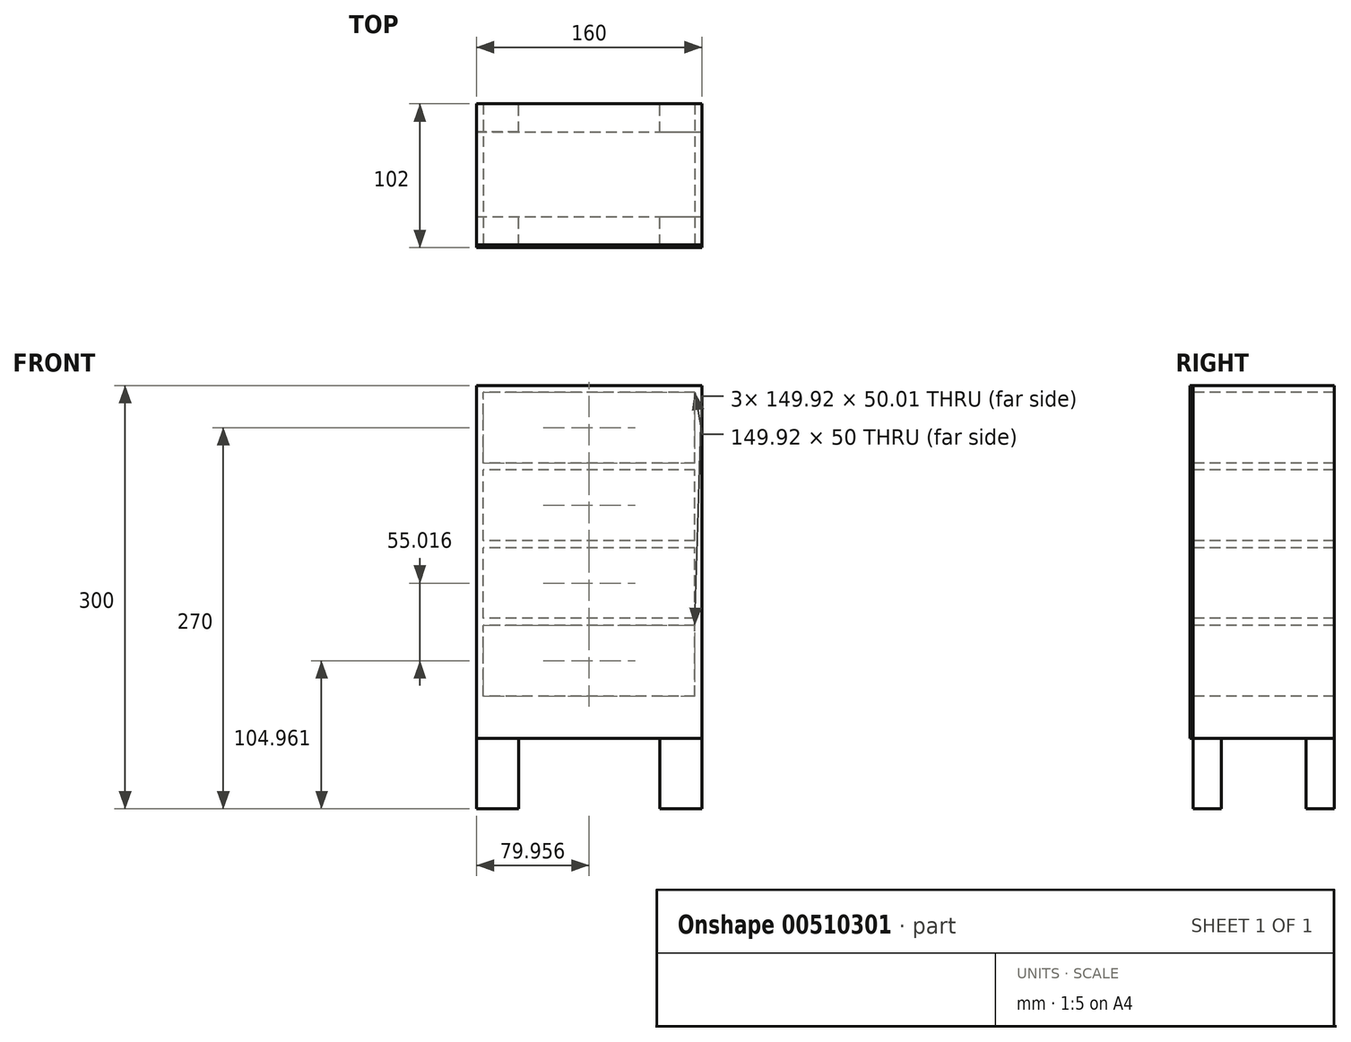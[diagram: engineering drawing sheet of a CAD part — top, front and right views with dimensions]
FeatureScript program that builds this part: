
annotation { "Feature Type Name" : "Feature", "Feature Type Description" : "" }
export const myFeature = defineFeature(function(context is Context, id is Id, definition is map)
    precondition{}
    {
        {
            var Q0;
            Q0=qCreatedBy(makeId("Front.planeOp"),FACE);
            var sketch = newSketch(context, id + "F0", { "sketchPlane" : qUnion([Q0])});
            skLineSegment(sketch, "E0.bottom", {"start": v(-78.04, -26.24) * mm, "end": v(-48.04, -26.24) * mm});
            skLineSegment(sketch, "E0.top", {"start": v(-78.04, -76.24) * mm, "end": v(-48.04, -76.24) * mm});
            skLineSegment(sketch, "E0.left", {"start": v(-78.04, -26.24) * mm, "end": v(-78.04, -76.24) * mm});
            skLineSegment(sketch, "E0.right", {"start": v(-48.04, -26.24) * mm, "end": v(-48.04, -76.24) * mm});
            skLineSegment(sketch, "E1.bottom", {"start": v(51.96, -26.2) * mm, "end": v(81.96, -26.2) * mm});
            skLineSegment(sketch, "E1.top", {"start": v(51.96, -76.21) * mm, "end": v(81.96, -76.21) * mm});
            skLineSegment(sketch, "E1.left", {"start": v(81.96, -26.2) * mm, "end": v(81.96, -76.21) * mm});
            skLineSegment(sketch, "E1.right", {"start": v(51.96, -26.2) * mm, "end": v(51.96, -76.21) * mm});
            skSolve(sketch);
        }
        {
            var Q0;
            Q0 = qSketchRegion(id + "F0", true);
            extrude(context, id + "F1", {"entities" : qUnion([Q0]), "endBound" : BoundingType.SYMMETRIC, "depth" : 100 * mm});
        }
        {
            var Q0;
            Q0=makeQuery(id+"F1.opExtrude","SWEPT_FACE",FACE,{"disambiguationData":[OSD([sQuery(id+"F0.wireOp",EDGE,"E0.bottom")])]});
            var sketch = newSketch(context, id + "F2", { "sketchPlane" : qUnion([Q0])});
            skLineSegment(sketch, "E2.bottom", {"start": v(-78.04, 50) * mm, "end": v(81.88, 50) * mm});
            skLineSegment(sketch, "E2.top", {"start": v(-78.04, -50) * mm, "end": v(81.88, -50) * mm});
            skLineSegment(sketch, "E2.left", {"start": v(-78.04, 50) * mm, "end": v(-78.04, -50) * mm});
            skLineSegment(sketch, "E2.right", {"start": v(81.88, 50) * mm, "end": v(81.88, -50) * mm});
            skSolve(sketch);
        }
        {
            var Q0;
            Q0 = qSketchRegion(id + "F2", true);
            extrude(context, id + "F3", {"entities" : qUnion([Q0]), "depth" : 250 * mm});
        }
        {
            var Q0;
            Q0=makeQuery(id+"F3.opExtrude","SWEPT_FACE",FACE,{"disambiguationData":[OSD([sQuery(id+"F2.wireOp",EDGE,"E2.top")])]});
            var sketch = newSketch(context, id + "F4", { "sketchPlane" : qUnion([Q0])});
            skLineSegment(sketch, "E3.bottom", {"start": v(-73.04, 218.76) * mm, "end": v(76.87, 218.76) * mm});
            skLineSegment(sketch, "E3.top", {"start": v(-73.04, 168.76) * mm, "end": v(76.87, 168.76) * mm});
            skLineSegment(sketch, "E3.left", {"start": v(-73.04, 218.76) * mm, "end": v(-73.04, 168.76) * mm});
            skLineSegment(sketch, "E3.right", {"start": v(76.87, 218.76) * mm, "end": v(76.87, 168.76) * mm});
            skSolve(sketch);
        }
        {
            var Q0;
            Q0=makeQuery(id+"F4.imprint","IMPRINT",FACE,{"disambiguationData":[TD([[makeQuery(id+"F4.imprint","IMPRINT",EDGE,{"derivedFrom":sQuery(id+"F4.wireOp",EDGE,"E3.bottom")}),-1.0]])]});
            extrude(context, id + "F5", {"entities" : qUnion([Q0]), "operationType" : NewBodyOperationType.REMOVE, "endBound" : BoundingType.THROUGH_ALL, "oppositeDirection" : true, "depth" : 152.4 * mm});
        }
        {
            var Q0;
            Q0=makeQuery(id+"F3.opExtrude","SWEPT_FACE",FACE,{"disambiguationData":[OSD([sQuery(id+"F2.wireOp",EDGE,"E2.top")])]});
            var sketch = newSketch(context, id + "F6", { "sketchPlane" : qUnion([Q0])});
            skLineSegment(sketch, "E4.bottom", {"start": v(-73.04, 163.76) * mm, "end": v(76.87, 163.76) * mm});
            skLineSegment(sketch, "E4.top", {"start": v(-73.04, 113.75) * mm, "end": v(76.87, 113.75) * mm});
            skLineSegment(sketch, "E4.left", {"start": v(-73.04, 163.76) * mm, "end": v(-73.04, 113.75) * mm});
            skLineSegment(sketch, "E4.right", {"start": v(76.87, 163.76) * mm, "end": v(76.87, 113.75) * mm});
            skSolve(sketch);
        }
        {
            var Q0;
            Q0=makeQuery(id+"F6.imprint","IMPRINT",FACE,{"disambiguationData":[TD([[makeQuery(id+"F6.imprint","IMPRINT",EDGE,{"derivedFrom":sQuery(id+"F6.wireOp",EDGE,"E4.bottom")}),-1.0]])]});
            extrude(context, id + "F7", {"entities" : qUnion([Q0]), "operationType" : NewBodyOperationType.REMOVE, "endBound" : BoundingType.THROUGH_ALL, "oppositeDirection" : true, "depth" : 25.4 * mm});
        }
        {
            var Q0;
            Q0=makeQuery(id+"F3.opExtrude","SWEPT_FACE",FACE,{"disambiguationData":[OSD([sQuery(id+"F2.wireOp",EDGE,"E2.top")])]});
            var sketch = newSketch(context, id + "F8", { "sketchPlane" : qUnion([Q0])});
            skLineSegment(sketch, "E5.bottom", {"start": v(-73.04, 108.74) * mm, "end": v(76.87, 108.74) * mm});
            skLineSegment(sketch, "E5.top", {"start": v(-73.04, 58.73) * mm, "end": v(76.87, 58.73) * mm});
            skLineSegment(sketch, "E5.left", {"start": v(-73.04, 108.74) * mm, "end": v(-73.04, 58.73) * mm});
            skLineSegment(sketch, "E5.right", {"start": v(76.87, 108.74) * mm, "end": v(76.87, 58.73) * mm});
            skSolve(sketch);
        }
        {
            var Q0;
            Q0=makeQuery(id+"F8.imprint","IMPRINT",FACE,{"disambiguationData":[TD([[makeQuery(id+"F8.imprint","IMPRINT",EDGE,{"derivedFrom":sQuery(id+"F8.wireOp",EDGE,"E5.bottom")}),-1.0]])]});
            extrude(context, id + "F9", {"entities" : qUnion([Q0]), "operationType" : NewBodyOperationType.REMOVE, "endBound" : BoundingType.THROUGH_ALL, "oppositeDirection" : true, "depth" : 25.4 * mm});
        }
        {
            var Q0;
            Q0=makeQuery(id+"F3.opExtrude","SWEPT_FACE",FACE,{"disambiguationData":[OSD([sQuery(id+"F2.wireOp",EDGE,"E2.top")])]});
            var sketch = newSketch(context, id + "F10", { "sketchPlane" : qUnion([Q0])});
            skLineSegment(sketch, "E6.bottom", {"start": v(-73.04, 53.73) * mm, "end": v(76.87, 53.73) * mm});
            skLineSegment(sketch, "E6.top", {"start": v(-73.04, 3.72) * mm, "end": v(76.87, 3.72) * mm});
            skLineSegment(sketch, "E6.left", {"start": v(-73.04, 53.73) * mm, "end": v(-73.04, 3.72) * mm});
            skLineSegment(sketch, "E6.right", {"start": v(76.87, 53.73) * mm, "end": v(76.87, 3.72) * mm});
            skSolve(sketch);
        }
        {
            var Q0;
            Q0=makeQuery(id+"F10.imprint","IMPRINT",FACE,{"disambiguationData":[TD([[makeQuery(id+"F10.imprint","IMPRINT",EDGE,{"derivedFrom":sQuery(id+"F10.wireOp",EDGE,"E6.bottom")}),-1.0]])]});
            extrude(context, id + "F11", {"entities" : qUnion([Q0]), "operationType" : NewBodyOperationType.REMOVE, "endBound" : BoundingType.THROUGH_ALL, "oppositeDirection" : true, "depth" : 25.4 * mm});
        }
        {
            var Q0;
            Q0=makeQuery(id+"F1.opExtrude","SWEPT_FACE",FACE,{"disambiguationData":[OSD([sQuery(id+"F0.wireOp",EDGE,"E1.left")])]});
            var sketch = newSketch(context, id + "F12", { "sketchPlane" : qUnion([Q0])});
            skLineSegment(sketch, "E7.bottom", {"start": v(-30, -26.2) * mm, "end": v(30.01, -26.2) * mm});
            skLineSegment(sketch, "E7.top", {"start": v(-30, -76.21) * mm, "end": v(30.01, -76.21) * mm});
            skLineSegment(sketch, "E7.left", {"start": v(-30, -26.2) * mm, "end": v(-30, -76.21) * mm});
            skLineSegment(sketch, "E7.right", {"start": v(30.01, -26.2) * mm, "end": v(30.01, -76.21) * mm});
            skSolve(sketch);
        }
        {
            var Q0;
            Q0 = qSketchRegion(id + "F12", true);
            extrude(context, id + "F13", {"entities" : qUnion([Q0]), "operationType" : NewBodyOperationType.REMOVE, "endBound" : BoundingType.THROUGH_ALL, "oppositeDirection" : true, "depth" : 25.4 * mm});
        }
        {
            var Q0;
            Q0=makeQuery(id+"F1.opExtrude","SWEPT_FACE",FACE,{"disambiguationData":[OSD([sQuery(id+"F0.wireOp",EDGE,"E0.left")])]});
            var sketch = newSketch(context, id + "F14", { "sketchPlane" : qUnion([Q0])});
            skLineSegment(sketch, "E8.bottom", {"start": v(-30, -26.24) * mm, "end": v(30, -26.24) * mm});
            skLineSegment(sketch, "E8.top", {"start": v(-30, -76.24) * mm, "end": v(30, -76.24) * mm});
            skLineSegment(sketch, "E8.left", {"start": v(-30, -26.24) * mm, "end": v(-30, -76.24) * mm});
            skLineSegment(sketch, "E8.right", {"start": v(30, -26.24) * mm, "end": v(30, -76.24) * mm});
            skSolve(sketch);
        }
        {
            var Q0;
            Q0 = qSketchRegion(id + "F14", true);
            extrude(context, id + "F15", {"entities" : qUnion([Q0]), "operationType" : NewBodyOperationType.REMOVE, "endBound" : BoundingType.THROUGH_ALL, "oppositeDirection" : true, "depth" : 25.4 * mm});
        }
        {
            var Q0;
            Q0=makeQuery(id+"F3.opExtrude","SWEPT_FACE",FACE,{"disambiguationData":[OSD([sQuery(id+"F2.wireOp",EDGE,"E2.top")])]});
            var sketch = newSketch(context, id + "F16", { "sketchPlane" : qUnion([Q0])});
            skLineSegment(sketch, "E9.bottom", {"start": v(-78.04, 223.76) * mm, "end": v(81.88, 223.76) * mm});
            skLineSegment(sketch, "E9.top", {"start": v(-78.04, -26.24) * mm, "end": v(81.88, -26.24) * mm});
            skLineSegment(sketch, "E9.left", {"start": v(-78.04, 223.76) * mm, "end": v(-78.04, -26.24) * mm});
            skLineSegment(sketch, "E9.right", {"start": v(81.88, 223.76) * mm, "end": v(81.88, -26.24) * mm});
            skSolve(sketch);
        }
        {
            var Q0;
            Q0 = qSketchRegion(id + "F16", true);
            extrude(context, id + "F17", {"entities" : qUnion([Q0]), "depth" : 2 * mm});
        }
    });
